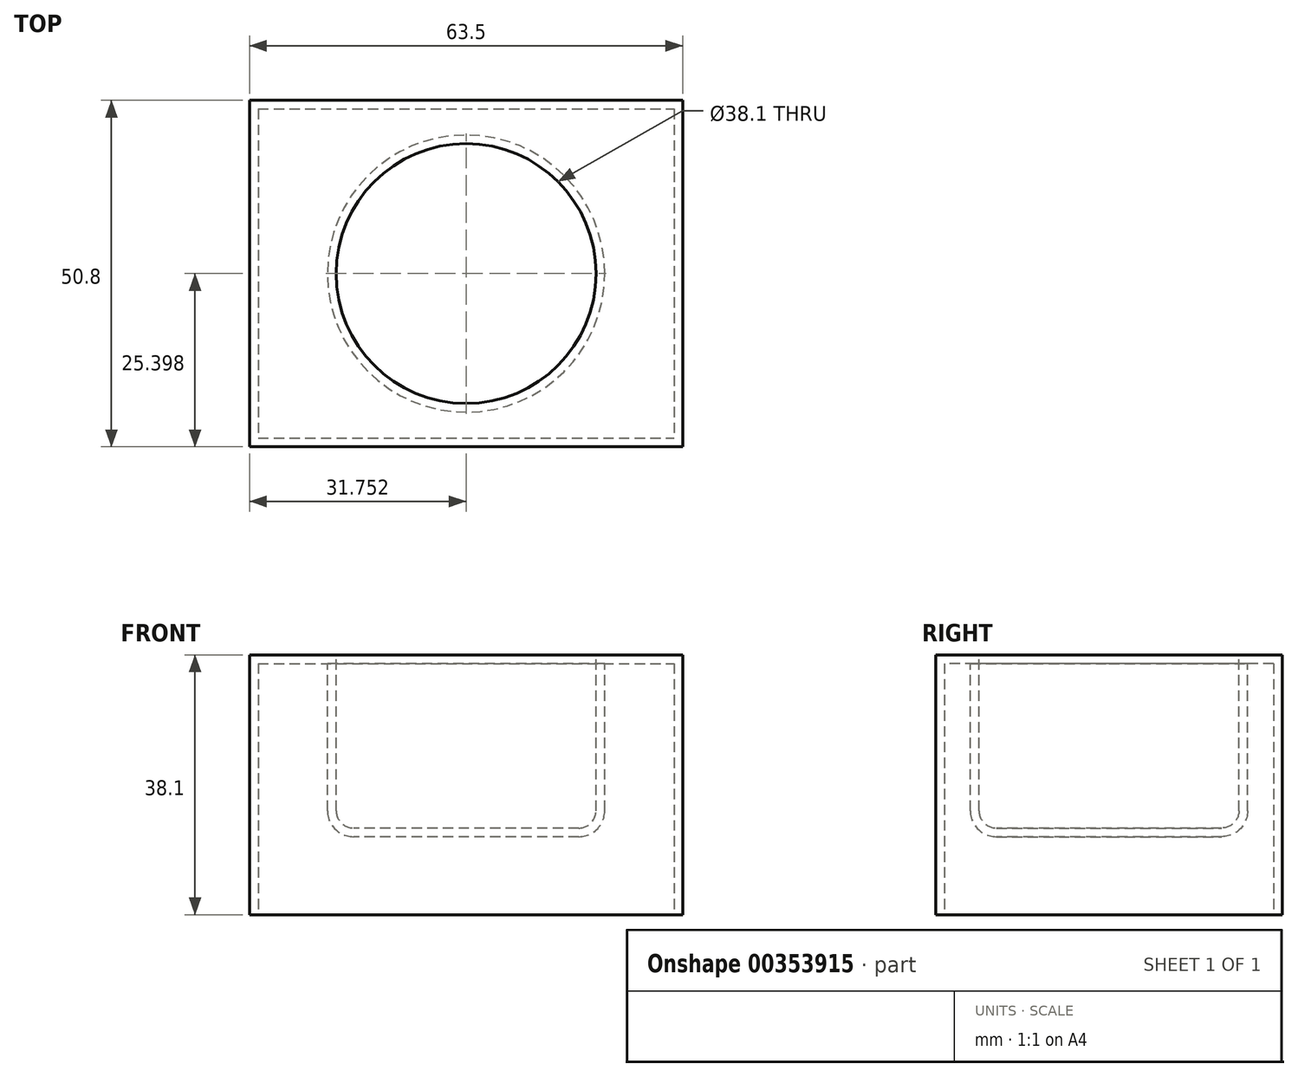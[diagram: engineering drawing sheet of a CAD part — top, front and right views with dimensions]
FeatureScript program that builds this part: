
annotation { "Feature Type Name" : "Feature", "Feature Type Description" : "" }
export const myFeature = defineFeature(function(context is Context, id is Id, definition is map)
    precondition{}
    {
        {
            var Q0;
            Q0=qCreatedBy(makeId("Top.planeOp"),FACE);
            var sketch = newSketch(context, id + "F0", { "sketchPlane" : qUnion([Q0])});
            skLineSegment(sketch, "E0.bottom", {"start": v(-34.9, 17.25) * mm, "end": v(28.6, 17.25) * mm});
            skLineSegment(sketch, "E0.top", {"start": v(-34.9, -33.55) * mm, "end": v(28.6, -33.55) * mm});
            skLineSegment(sketch, "E0.left", {"start": v(-34.9, 17.25) * mm, "end": v(-34.9, -33.55) * mm});
            skLineSegment(sketch, "E0.right", {"start": v(28.6, 17.25) * mm, "end": v(28.6, -33.55) * mm});
            skSolve(sketch);
        }
        {
            var Q0;
            Q0 = qSketchRegion(id + "F0", true);
            extrude(context, id + "F1", {"entities" : qUnion([Q0]), "depth" : 38.1 * mm});
        }
        {
            var Q0;
            Q0=makeQuery(id+"F1.opExtrude","CAP_FACE",FACE,{"disambiguationData":[OSD([sQuery(id+"F0.wireOp",EDGE,"E0.bottom"),sQuery(id+"F0.wireOp",EDGE,"E0.top"),sQuery(id+"F0.wireOp",EDGE,"E0.left"),sQuery(id+"F0.wireOp",EDGE,"E0.right")])],"isStart":false});
            var sketch = newSketch(context, id + "F2", { "sketchPlane" : qUnion([Q0])});
            skLineSegment(sketch, "E1", {"start": v(-34.9, 17.25) * mm, "end": v(28.6, -33.55) * mm, "construction": true});
            skCircle(sketch, "E2", {"center": v(-3.15, -8.15) * mm, "radius": 19.05 * mm});
            skSolve(sketch);
        }
        {
            var Q0;
            Q0=makeQuery(id+"F2.imprint","IMPRINT",FACE,{"disambiguationData":[TD([[makeQuery(id+"F2.imprint","IMPRINT",EDGE,{"derivedFrom":sQuery(id+"F2.wireOp",EDGE,"E2")}),1.0]])]});
            var Q1;
            Q1=sQuery(id+"F2.wireOp",EDGE,"E2");
            extrude(context, id + "F3", {"entities" : qUnion([Q0]), "operationType" : NewBodyOperationType.REMOVE, "surfaceEntities" : qUnion([Q1]), "oppositeDirection" : true, "depth" : 25.4 * mm});
        }
        {
            var Q0;
            Q0=makeQuery(id+"F3.boolean.opBoolean","COPY",EDGE,{"derivedFrom":makeQuery(id+"F3.opExtrude","CAP_EDGE",EDGE,{"disambiguationData":[OSD([sQuery(id+"F2.wireOp",EDGE,"E2")])],"isStart":false})});
            fillet(context, id + "F4", {"entities" : qUnion([Q0]), "radius" : 2.54 * mm, "tangentPropagation" : true, "allowEdgeOverflow" : false});
        }
        {
            var Q0;
            Q0=makeQuery(id+"F1.opExtrude","CAP_FACE",FACE,{"disambiguationData":[OSD([sQuery(id+"F0.wireOp",EDGE,"E0.bottom"),sQuery(id+"F0.wireOp",EDGE,"E0.top"),sQuery(id+"F0.wireOp",EDGE,"E0.left"),sQuery(id+"F0.wireOp",EDGE,"E0.right")])],"isStart":true});
            shell(context, id + "F5", {"entities" : qUnion([Q0]), "thickness" : 1.27 * mm});
        }
    });
